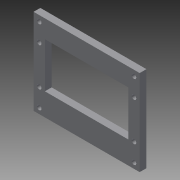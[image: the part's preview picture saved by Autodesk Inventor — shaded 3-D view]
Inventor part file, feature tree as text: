
AUTODESK INVENTOR PART (.ipt)
format: ipt  version: 2015 (Build 190159000, 159)  size: 112,640 bytes
history: native  units: in
note: dims shown in document units (in); Inventor stores cm internally (conversion verified against a paired STEP export)
features: extrude x3, sketch x3, plane x1, reference x1
ambient origin geometry x8: Origin, YZ Plane, XZ Plane, XY Plane, X Axis, Y Axis, Z Axis, Center Point
bodies: Solid1 (feature_tree)
feature tree (8):
  plane  "Work Plane1"
  extrude  "Extrusion1"  Depth=0.1969in
  extrude  "Extrusion2"  Depth=0.1181in TaperAngle=0.0deg
  extrude  "Extrusion3"  Depth=0.1181in
  sketch  "Sketch1"  dims[d0=0.1181in d1=0.0in d2=0.1969in]
  reference  "Reference1"
  sketch  "Sketch2"  dims[d3=0.1969in d4=0.1181in d5=0.0in]
  sketch  "Sketch4"  dims[d6=0.0984in d7=0.0984in d8=0.0984in d9=0.0984in d10=0.1181in d11=0.0in]
